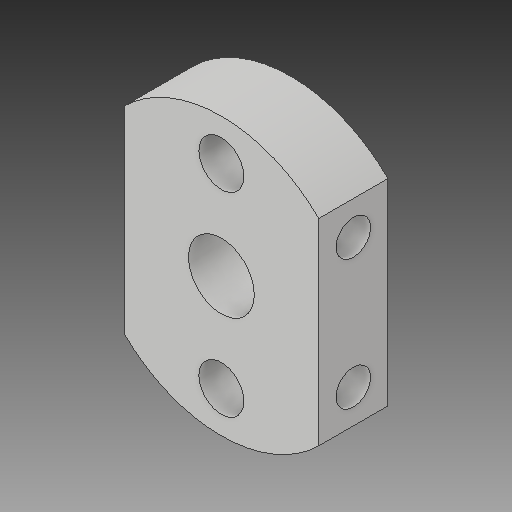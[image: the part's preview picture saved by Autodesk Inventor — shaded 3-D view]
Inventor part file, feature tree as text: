
AUTODESK INVENTOR PART (.ipt)
format: ipt  version: 2019 (Build 230136000, 136)  size: 148,992 bytes
history: native  units: in
note: dims shown in document units (in); Inventor stores cm internally (conversion verified against a paired STEP export)
features: sketch x5, hole x3, extrude x2, plane x1, mirror x1, projected_geometry x1
ambient origin geometry x8: Origin, YZ Plane, XZ Plane, XY Plane, X Axis, Y Axis, Z Axis, Center Point
bodies: Solid1 (feature_tree)
feature tree (13):
  extrude  "Extrusion1"  Depth=0.4in TaperAngle=0.0deg
  hole  "Hole1"  [1 undecoded]
  hole  "Hole2"  [1 undecoded]
  extrude  "Extrusion2"  Depth=0.4in TaperAngle=0.0deg
  hole  "Hole3"  [1 undecoded]
  plane  "Work Plane1"
  mirror  "Mirror1"
  sketch  "Sketch1"  dims[d0=1.6in d1=0.4in d2=0.0in]
  sketch  "Sketch2"  dims[d3=0.38in d4=0.276in d5=0.438in d6=0.25in d7=0.5635in d8=0.432in d9=0.8108in d10=1.125in]
  sketch  "Sketch3"  dims[d11=0.5625in]
  sketch  "Sketch4"  dims[d12=0.26in d13=0.276in d14=0.281in d15=0.138in d16=0.5635in d17=0.432in d18=0.8108in d19=1.125in]
  sketch  "Sketch5"  dims[d20=0.5625in d21=0.4in d22=0.0in d23=0.4in d24=0.2in d25=0.2in d26=0.75in d27=1.1377in d28=0.1939in d29=0.2in d30=0.75in d31=0.375in d32=0.25in d33=0.5635in d34=0.432in d35=0.8108in]
  projected_geometry  "Projected Loop1"
note: 3 required parameter values undecoded (feature->parameter linkage not recoverable at this tier; creation-order binding heuristic only, values carry confidence <= 0.55)
